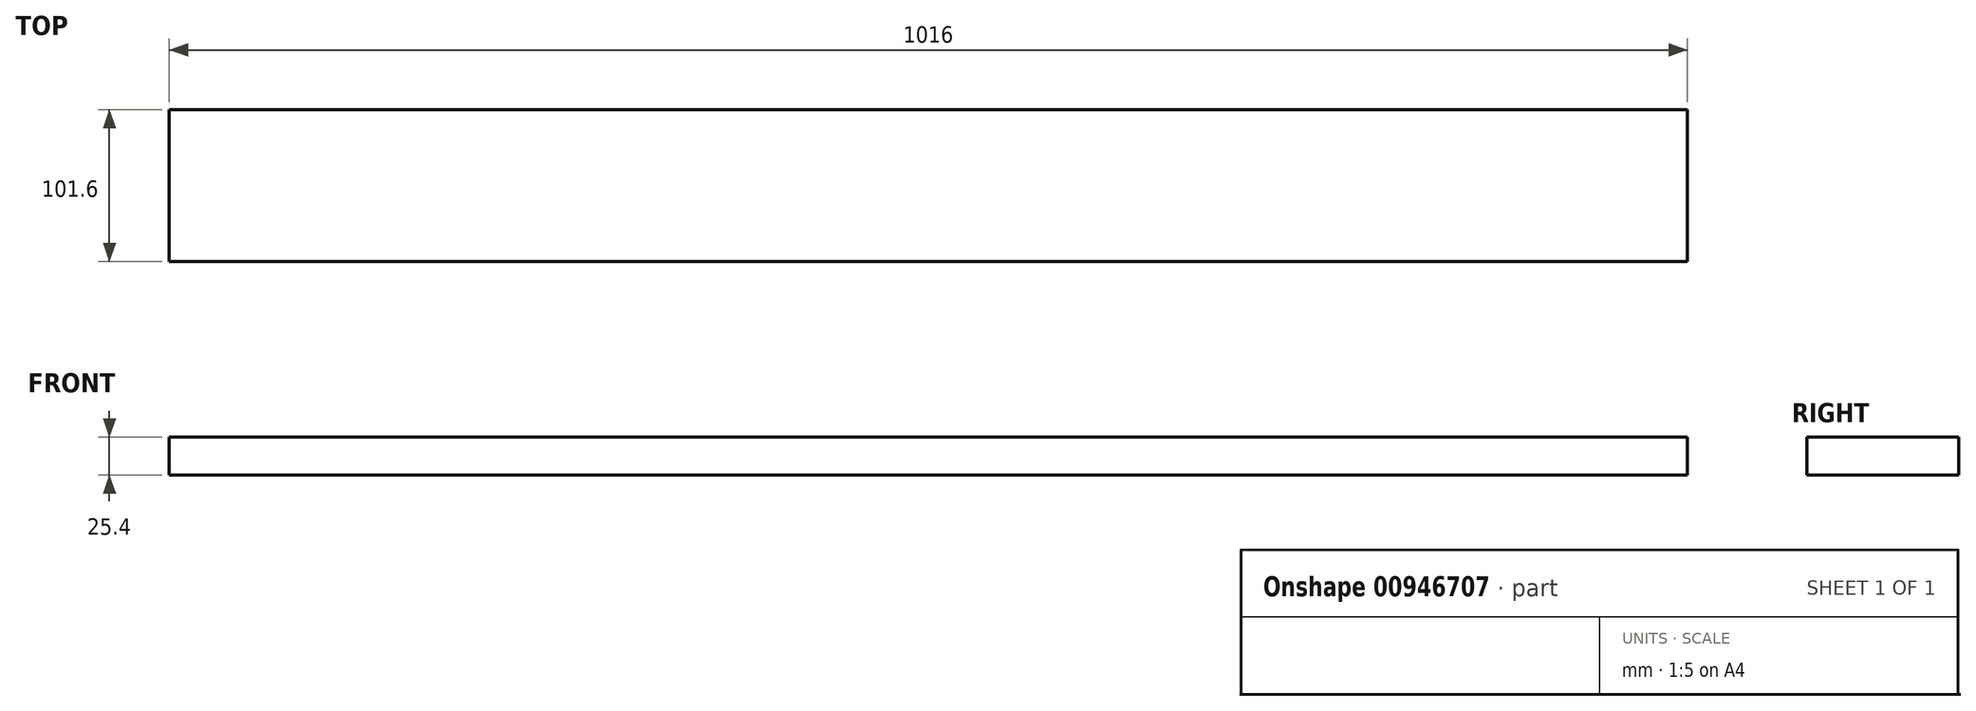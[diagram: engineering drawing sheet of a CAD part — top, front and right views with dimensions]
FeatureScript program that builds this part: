
annotation { "Feature Type Name" : "Feature", "Feature Type Description" : "" }
export const myFeature = defineFeature(function(context is Context, id is Id, definition is map)
    precondition{}
    {
        {
            var Q0;
            Q0=qCreatedBy(makeId("Top.planeOp"),FACE);
            var sketch = newSketch(context, id + "F0", { "sketchPlane" : qUnion([Q0])});
            skLineSegment(sketch, "E0.bottom", {"start": v(508, 50.8) * mm, "end": v(-508, 50.8) * mm});
            skLineSegment(sketch, "E0.top", {"start": v(508, -50.8) * mm, "end": v(-508, -50.8) * mm});
            skLineSegment(sketch, "E0.left", {"start": v(508, 50.8) * mm, "end": v(508, -50.8) * mm});
            skLineSegment(sketch, "E0.right", {"start": v(-508, 50.8) * mm, "end": v(-508, -50.8) * mm});
            skPoint(sketch, "E0.middle", {"position": v(0, 0) * mm});
            skSolve(sketch);
        }
        {
            var Q0;
            Q0=qSketchRegion(id+"F0",true);
            extrude(context, id + "F1", {"entities" : qUnion([Q0]), "depth" : 25.4 * mm, "offsetDistance" : 25.4 * mm});
        }
    });
